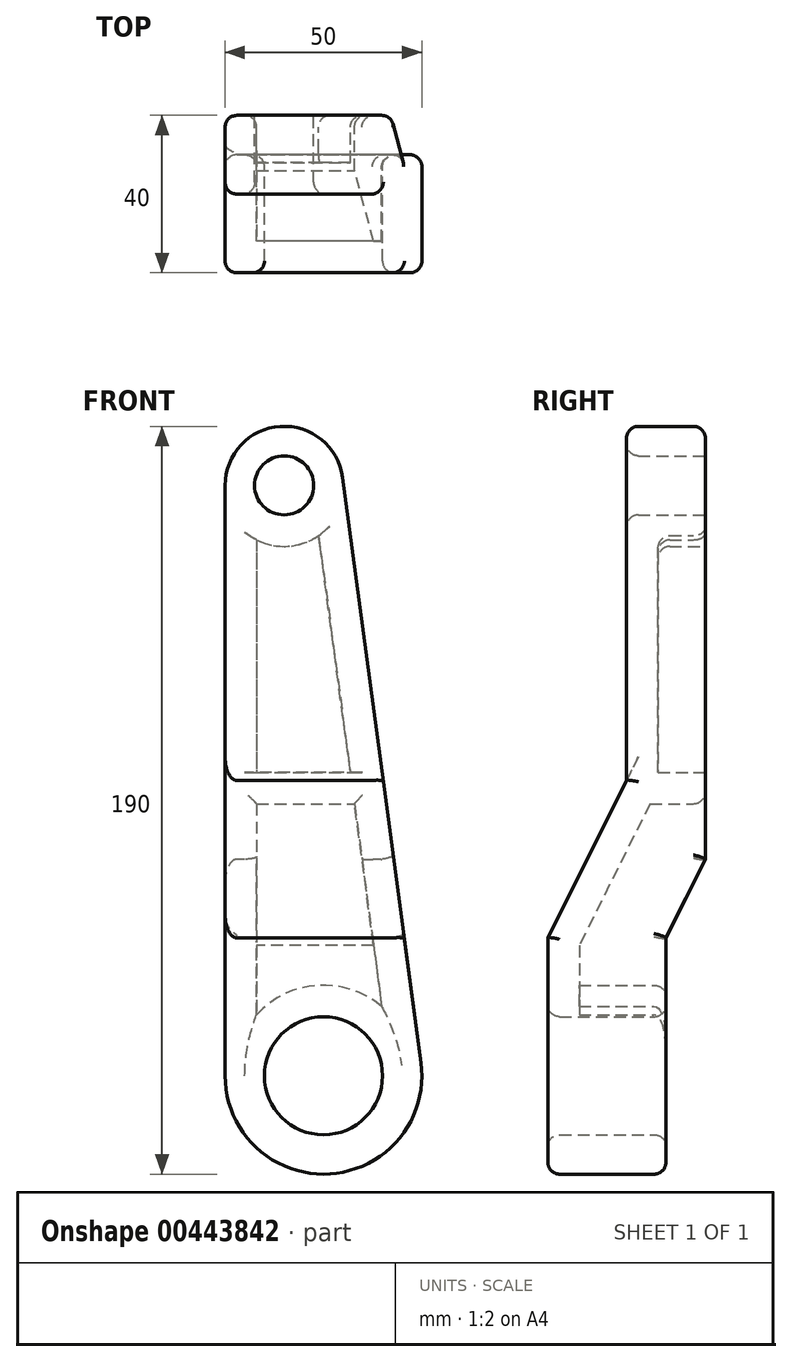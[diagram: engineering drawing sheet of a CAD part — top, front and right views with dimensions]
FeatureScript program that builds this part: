
annotation { "Feature Type Name" : "Feature", "Feature Type Description" : "" }
export const myFeature = defineFeature(function(context is Context, id is Id, definition is map)
    precondition{}
    {
        {
            var Q0;
            Q0=qCreatedBy(makeId("Front.planeOp"),FACE);
            var sketch = newSketch(context, id + "F0", { "sketchPlane" : qUnion([Q0])});
            skArc(sketch, "E0", {"start": v(-25, 0) * mm, "mid": v(1.66, -24.94) * mm, "end": v(24.78, 3.32) * mm});
            skArc(sketch, "E1", {"start": v(4.87, 152) * mm, "mid": v(-11, 164.97) * mm, "end": v(-25, 150) * mm});
            skLineSegment(sketch, "E2", {"start": v(-25, 150) * mm, "end": v(-25, 0) * mm});
            skLineSegment(sketch, "E3", {"start": v(4.87, 152) * mm, "end": v(24.78, 3.32) * mm});
            skSolve(sketch);
        }
        {
            var Q0;
            Q0=makeQuery(id+"F0.imprint","IMPRINT",FACE,{"disambiguationData":[TD([[makeQuery(id+"F0.imprint","IMPRINT",EDGE,{"derivedFrom":sQuery(id+"F0.wireOp",EDGE,"E0")}),1.0]])]});
            extrude(context, id + "F1", {"entities" : qUnion([Q0]), "depth" : 40 * mm});
        }
        {
            var Q0;
            Q0=makeQuery(id+"F1.opExtrude","SWEPT_FACE",FACE,{"disambiguationData":[OSD([sQuery(id+"F0.wireOp",EDGE,"E2")])]});
            var sketch = newSketch(context, id + "F2", { "sketchPlane" : qUnion([Q0])});
            skLineSegment(sketch, "E4", {"start": v(0, 55) * mm, "end": v(0, -25.94) * mm});
            skLineSegment(sketch, "E5", {"start": v(10, -25.94) * mm, "end": v(10, 35) * mm});
            skLineSegment(sketch, "E6", {"start": v(10, 35) * mm, "end": v(0, 55) * mm});
            skLineSegment(sketch, "E7", {"start": v(40, 35) * mm, "end": v(40, 165.97) * mm});
            skLineSegment(sketch, "E8", {"start": v(20, 165.97) * mm, "end": v(20, 75) * mm});
            skLineSegment(sketch, "E9", {"start": v(20, 75) * mm, "end": v(40, 35) * mm});
            skLineSegment(sketch, "E10", {"start": v(0, -25.94) * mm, "end": v(10, -25.94) * mm});
            skLineSegment(sketch, "E11", {"start": v(40, 165.97) * mm, "end": v(20, 165.97) * mm});
            skSolve(sketch);
        }
        {
            var Q0;
            Q0 = qSketchRegion(id + "F2", true);
            extrude(context, id + "F3", {"entities" : qUnion([Q0]), "operationType" : NewBodyOperationType.REMOVE, "endBound" : BoundingType.THROUGH_ALL, "oppositeDirection" : true, "depth" : 25 * mm});
        }
        {
            var Q0;
            Q0=makeQuery(id+"F1.opExtrude","CAP_FACE",FACE,{"disambiguationData":[OSD([sQuery(id+"F0.wireOp",EDGE,"E0"),sQuery(id+"F0.wireOp",EDGE,"E1"),sQuery(id+"F0.wireOp",EDGE,"E2"),sQuery(id+"F0.wireOp",EDGE,"E3")])],"isStart":true});
            var sketch = newSketch(context, id + "F4", { "sketchPlane" : qUnion([Q0])});
            skCircle(sketch, "E12", {"center": v(10, 150) * mm, "radius": 7.5 * mm});
            skCircle(sketch, "E13", {"center": v(0, 0) * mm, "radius": 15 * mm});
            skSolve(sketch);
        }
        {
            var Q0;
            Q0 = qSketchRegion(id + "F4", true);
            extrude(context, id + "F5", {"entities" : qUnion([Q0]), "operationType" : NewBodyOperationType.REMOVE, "endBound" : BoundingType.THROUGH_ALL, "oppositeDirection" : true, "depth" : 25 * mm});
        }
        {
            var Q0;
            Q0=makeQuery(id+"F1.opExtrude","CAP_FACE",FACE,{"disambiguationData":[OSD([sQuery(id+"F0.wireOp",EDGE,"E0"),sQuery(id+"F0.wireOp",EDGE,"E1"),sQuery(id+"F0.wireOp",EDGE,"E2"),sQuery(id+"F0.wireOp",EDGE,"E3")])],"isStart":true});
            var Q1;
            Q1=makeQuery(id+"F3.boolean.opBoolean","COPY",FACE,{"derivedFrom":makeQuery(id+"F3.opExtrude","SWEPT_FACE",FACE,{"disambiguationData":[OSD([sQuery(id+"F2.wireOp",EDGE,"E6")])]})});
            var Q2;
            Q2=makeQuery(id+"F3.boolean.opBoolean","COPY",FACE,{"derivedFrom":makeQuery(id+"F3.opExtrude","SWEPT_FACE",FACE,{"disambiguationData":[OSD([sQuery(id+"F2.wireOp",EDGE,"E5")])]})});
            shell(context, id + "F6", {"entities" : qUnion([Q0, Q1, Q2]), "thickness" : 8 * mm});
        }
        {
            var Q0;
            Q0=makeQuery(id+"F1.opExtrude","CAP_FACE",FACE,{"disambiguationData":[OSD([sQuery(id+"F0.wireOp",EDGE,"E0"),sQuery(id+"F0.wireOp",EDGE,"E1"),sQuery(id+"F0.wireOp",EDGE,"E2"),sQuery(id+"F0.wireOp",EDGE,"E3")])],"isStart":true});
            var sketch = newSketch(context, id + "F7", { "sketchPlane" : qUnion([Q0])});
            skLineSegment(sketch, "E14", {"start": v(-7.9, 69.11) * mm, "end": v(17, 69.11) * mm});
            skLineSegment(sketch, "E15", {"start": v(-6.82, 77.11) * mm, "end": v(17, 77.11) * mm});
            skLineSegment(sketch, "E16.0", {"start": v(-6.82, 77.11) * mm, "end": v(-7.9, 69.11) * mm});
            skPoint(sketch, "E17.orphan", {"position": v(1.23, 137.22) * mm});
            skPoint(sketch, "E18.orphan", {"position": v(17, 136.17) * mm});
            skPoint(sketch, "E19.orphan", {"position": v(17, 55) * mm});
            skPoint(sketch, "E20.orphan", {"position": v(-9.79, 55) * mm});
            skLineSegment(sketch, "E21", {"start": v(17, 77.11) * mm, "end": v(17, 69.11) * mm});
            skSolve(sketch);
        }
        {
            var Q0;
            Q0 = qSketchRegion(id + "F7", true);
            extrude(context, id + "F8", {"entities" : qUnion([Q0]), "operationType" : NewBodyOperationType.ADD, "endBound" : BoundingType.UP_TO_NEXT, "oppositeDirection" : true, "depth" : 8 * mm});
        }
        {
            var Q0;
            Q0=makeQuery(id+"F1.opExtrude","CAP_EDGE",EDGE,{"disambiguationData":[OSD([sQuery(id+"F0.wireOp",EDGE,"E3")])],"isStart":true});
            var Q1;
            Q1=makeQuery(id+"F1.opExtrude","CAP_EDGE",EDGE,{"disambiguationData":[OSD([sQuery(id+"F0.wireOp",EDGE,"E1")])],"isStart":true});
            var Q2;
            Q2=makeQuery(id+"F5.boolean.opBoolean","COPY",EDGE,{"derivedFrom":makeQuery(id+"F5.opExtrude","CAP_EDGE",EDGE,{"disambiguationData":[OSD([sQuery(id+"F4.wireOp",EDGE,"E12")])],"isStart":true})});
            var Q3;
            Q3=makeQuery(id+"F1.opExtrude","CAP_EDGE",EDGE,{"disambiguationData":[OSD([sQuery(id+"F0.wireOp",EDGE,"E2")])],"isStart":true});
            var Q4;
            Q4=makeQuery(id+"F6.opShell","OFFSET_EDGE",EDGE,{"disambiguationData":[OSD([sQuery(id+"F4.wireOp",EDGE,"E12")])]});
            var Q5;
            {var subQ1=sQuery(id+"F0.wireOp",EDGE,"E2");Q5=makeQuery(id+"F8.boolean.opBoolean","SPLIT",EDGE,{"disambiguationData":[TD([makeQuery(id+"F6.opShell","OFFSET_FACE",FACE,{"disambiguationData":[OSD([sQuery(id+"F4.wireOp",EDGE,"E12")])]})])],"derivedFrom":makeQuery(id+"F6.opShell","OFFSET_EDGE",EDGE,{"disambiguationData":[OSD([subQ1]),TDD([makeQuery(id+"F1.opExtrude","CAP_EDGE",EDGE,{"disambiguationData":[OSD([subQ1])],"isStart":true})])]})});}
            var Q6;
            {var subQ1=sQuery(id+"F0.wireOp",EDGE,"E3");Q6=makeQuery(id+"F8.boolean.opBoolean","SPLIT",EDGE,{"disambiguationData":[TD([makeQuery(id+"F6.opShell","OFFSET_FACE",FACE,{"disambiguationData":[OSD([sQuery(id+"F4.wireOp",EDGE,"E12")])]})])],"derivedFrom":makeQuery(id+"F6.opShell","OFFSET_EDGE",EDGE,{"disambiguationData":[OSD([subQ1]),TDD([makeQuery(id+"F1.opExtrude","CAP_EDGE",EDGE,{"disambiguationData":[OSD([subQ1])],"isStart":true})])]})});}
            var Q7;
            Q7=makeQuery(id+"F5.boolean.opBoolean","INTERSECT",EDGE,{"derivedFrom":[makeQuery(id+"F3.boolean.opBoolean","COPY",FACE,{"derivedFrom":makeQuery(id+"F3.opExtrude","SWEPT_FACE",FACE,{"disambiguationData":[OSD([sQuery(id+"F2.wireOp",EDGE,"E5")])]})}),makeQuery(id+"F5.opExtrude","SWEPT_FACE",FACE,{"disambiguationData":[OSD([sQuery(id+"F4.wireOp",EDGE,"E13")])]})]});
            var Q8;
            Q8=makeQuery(id+"F6.opShell","OFFSET_EDGE",EDGE,{"disambiguationData":[OSD([sQuery(id+"F2.wireOp",EDGE,"E5"),sQuery(id+"F4.wireOp",EDGE,"E13")])]});
            var Q9;
            Q9=makeQuery(id+"F3.boolean.opBoolean","INTERSECT",EDGE,{"derivedFrom":[makeQuery(id+"F1.opExtrude","SWEPT_FACE",FACE,{"disambiguationData":[OSD([sQuery(id+"F0.wireOp",EDGE,"E0")])]}),makeQuery(id+"F3.opExtrude","SWEPT_FACE",FACE,{"disambiguationData":[OSD([sQuery(id+"F2.wireOp",EDGE,"E5")])]})]});
            var Q10;
            Q10=makeQuery(id+"F3.boolean.opBoolean","COPY",EDGE,{"derivedFrom":makeQuery(id+"F3.opExtrude","CAP_EDGE",EDGE,{"disambiguationData":[OSD([sQuery(id+"F2.wireOp",EDGE,"E5")])],"isStart":true})});
            var Q11;
            Q11=makeQuery(id+"F3.boolean.opBoolean","INTERSECT",EDGE,{"derivedFrom":[makeQuery(id+"F1.opExtrude","SWEPT_FACE",FACE,{"disambiguationData":[OSD([sQuery(id+"F0.wireOp",EDGE,"E3")])]}),makeQuery(id+"F3.opExtrude","SWEPT_FACE",FACE,{"disambiguationData":[OSD([sQuery(id+"F2.wireOp",EDGE,"E5")])]})]});
            var Q12;
            Q12=makeQuery(id+"F3.boolean.opBoolean","INTERSECT",EDGE,{"derivedFrom":[makeQuery(id+"F1.opExtrude","SWEPT_FACE",FACE,{"disambiguationData":[OSD([sQuery(id+"F0.wireOp",EDGE,"E3")])]}),makeQuery(id+"F3.opExtrude","SWEPT_FACE",FACE,{"disambiguationData":[OSD([sQuery(id+"F2.wireOp",EDGE,"E6")])]})]});
            var Q13;
            Q13=makeQuery(id+"F6.opShell","OFFSET_EDGE",EDGE,{"disambiguationData":[OSD([sQuery(id+"F0.wireOp",EDGE,"E3"),sQuery(id+"F2.wireOp",EDGE,"E6")])]});
            var Q14;
            {var subQ0=sQuery(id+"F0.wireOp",EDGE,"E3");Q14=makeQuery(id+"F8.boolean.opBoolean","SPLIT",EDGE,{"disambiguationData":[TD([makeQuery(id+"F6.opShell","OFFSET_FACE",FACE,{"disambiguationData":[OSD([sQuery(id+"F2.wireOp",EDGE,"E6")])]})])],"derivedFrom":makeQuery(id+"F6.opShell","OFFSET_EDGE",EDGE,{"disambiguationData":[OSD([subQ0]),TDD([makeQuery(id+"F1.opExtrude","CAP_EDGE",EDGE,{"disambiguationData":[OSD([subQ0])],"isStart":true})])]})});}
            var Q15;
            Q15=makeQuery(id+"F8.opExtrude","CAP_EDGE",EDGE,{"disambiguationData":[OSD([sQuery(id+"F7.wireOp",EDGE,"E14")])],"isStart":true});
            var Q16;
            {var subQ0=sQuery(id+"F0.wireOp",EDGE,"E2");Q16=makeQuery(id+"F8.boolean.opBoolean","SPLIT",EDGE,{"disambiguationData":[TD([makeQuery(id+"F3.boolean.opBoolean","COPY",FACE,{"derivedFrom":makeQuery(id+"F3.opExtrude","SWEPT_FACE",FACE,{"disambiguationData":[OSD([sQuery(id+"F2.wireOp",EDGE,"E6")])]})})])],"derivedFrom":makeQuery(id+"F6.opShell","OFFSET_EDGE",EDGE,{"disambiguationData":[OSD([subQ0]),TDD([makeQuery(id+"F1.opExtrude","CAP_EDGE",EDGE,{"disambiguationData":[OSD([subQ0])],"isStart":true})])]})});}
            var Q17;
            Q17=makeQuery(id+"F6.opShell","OFFSET_EDGE",EDGE,{"disambiguationData":[OSD([sQuery(id+"F2.wireOp",EDGE,"E6")])]});
            var Q18;
            Q18=makeQuery(id+"F3.boolean.opBoolean","COPY",EDGE,{"derivedFrom":makeQuery(id+"F3.opExtrude","CAP_EDGE",EDGE,{"disambiguationData":[OSD([sQuery(id+"F2.wireOp",EDGE,"E6")])],"isStart":true})});
            var Q19;
            Q19=makeQuery(id+"F6.opShell","OFFSET_EDGE",EDGE,{"disambiguationData":[OSD([sQuery(id+"F2.wireOp",EDGE,"E5")])]});
            var Q20;
            Q20=makeQuery(id+"F6.opShell","OFFSET_EDGE",EDGE,{"disambiguationData":[OSD([sQuery(id+"F0.wireOp",EDGE,"E3"),sQuery(id+"F2.wireOp",EDGE,"E5")])]});
            var Q21;
            Q21=makeQuery(id+"F1.opExtrude","CAP_EDGE",EDGE,{"disambiguationData":[OSD([sQuery(id+"F0.wireOp",EDGE,"E0")])],"isStart":false});
            var Q22;
            Q22=makeQuery(id+"F1.opExtrude","CAP_EDGE",EDGE,{"disambiguationData":[OSD([sQuery(id+"F0.wireOp",EDGE,"E3")])],"isStart":false});
            var Q23;
            Q23=makeQuery(id+"F3.boolean.opBoolean","INTERSECT",EDGE,{"derivedFrom":[makeQuery(id+"F1.opExtrude","SWEPT_FACE",FACE,{"disambiguationData":[OSD([sQuery(id+"F0.wireOp",EDGE,"E3")])]}),makeQuery(id+"F3.opExtrude","SWEPT_FACE",FACE,{"disambiguationData":[OSD([sQuery(id+"F2.wireOp",EDGE,"E9")])]})]});
            var Q24;
            Q24=makeQuery(id+"F3.boolean.opBoolean","INTERSECT",EDGE,{"derivedFrom":[makeQuery(id+"F1.opExtrude","SWEPT_FACE",FACE,{"disambiguationData":[OSD([sQuery(id+"F0.wireOp",EDGE,"E3")])]}),makeQuery(id+"F3.opExtrude","SWEPT_FACE",FACE,{"disambiguationData":[OSD([sQuery(id+"F2.wireOp",EDGE,"E8")])]})]});
            var Q25;
            Q25=makeQuery(id+"F3.boolean.opBoolean","INTERSECT",EDGE,{"derivedFrom":[makeQuery(id+"F1.opExtrude","SWEPT_FACE",FACE,{"disambiguationData":[OSD([sQuery(id+"F0.wireOp",EDGE,"E1")])]}),makeQuery(id+"F3.opExtrude","SWEPT_FACE",FACE,{"disambiguationData":[OSD([sQuery(id+"F2.wireOp",EDGE,"E8")])]})]});
            var Q26;
            Q26=makeQuery(id+"F3.boolean.opBoolean","COPY",EDGE,{"derivedFrom":makeQuery(id+"F3.opExtrude","CAP_EDGE",EDGE,{"disambiguationData":[OSD([sQuery(id+"F2.wireOp",EDGE,"E8")])],"isStart":true})});
            var Q27;
            Q27=makeQuery(id+"F3.boolean.opBoolean","COPY",EDGE,{"derivedFrom":makeQuery(id+"F3.opExtrude","CAP_EDGE",EDGE,{"disambiguationData":[OSD([sQuery(id+"F2.wireOp",EDGE,"E9")])],"isStart":true})});
            var Q28;
            Q28=makeQuery(id+"F1.opExtrude","CAP_EDGE",EDGE,{"disambiguationData":[OSD([sQuery(id+"F0.wireOp",EDGE,"E2")])],"isStart":false});
            var Q29;
            Q29=makeQuery(id+"F5.boolean.opBoolean","INTERSECT",EDGE,{"derivedFrom":[makeQuery(id+"F1.opExtrude","CAP_FACE",FACE,{"disambiguationData":[OSD([sQuery(id+"F0.wireOp",EDGE,"E0"),sQuery(id+"F0.wireOp",EDGE,"E1"),sQuery(id+"F0.wireOp",EDGE,"E2"),sQuery(id+"F0.wireOp",EDGE,"E3")])],"isStart":false}),makeQuery(id+"F5.opExtrude","SWEPT_FACE",FACE,{"disambiguationData":[OSD([sQuery(id+"F4.wireOp",EDGE,"E13")])]})]});
            var Q30;
            Q30=makeQuery(id+"F5.boolean.opBoolean","INTERSECT",EDGE,{"derivedFrom":[makeQuery(id+"F3.boolean.opBoolean","COPY",FACE,{"derivedFrom":makeQuery(id+"F3.opExtrude","SWEPT_FACE",FACE,{"disambiguationData":[OSD([sQuery(id+"F2.wireOp",EDGE,"E8")])]})}),makeQuery(id+"F5.opExtrude","SWEPT_FACE",FACE,{"disambiguationData":[OSD([sQuery(id+"F4.wireOp",EDGE,"E12")])]})]});
            fillet(context, id + "F9", {"entities" : qUnion([Q0, Q1, Q2, Q3, Q4, Q5, Q6, Q7, Q8, Q9, Q10, Q11, Q12, Q13, Q14, Q15, Q16, Q17, Q18, Q19, Q20, Q21, Q22, Q23, Q24, Q25, Q26, Q27, Q28, Q29, Q30]), "radius" : 3 * mm, "tangentPropagation" : true, "allowEdgeOverflow" : false});
        }
    });
